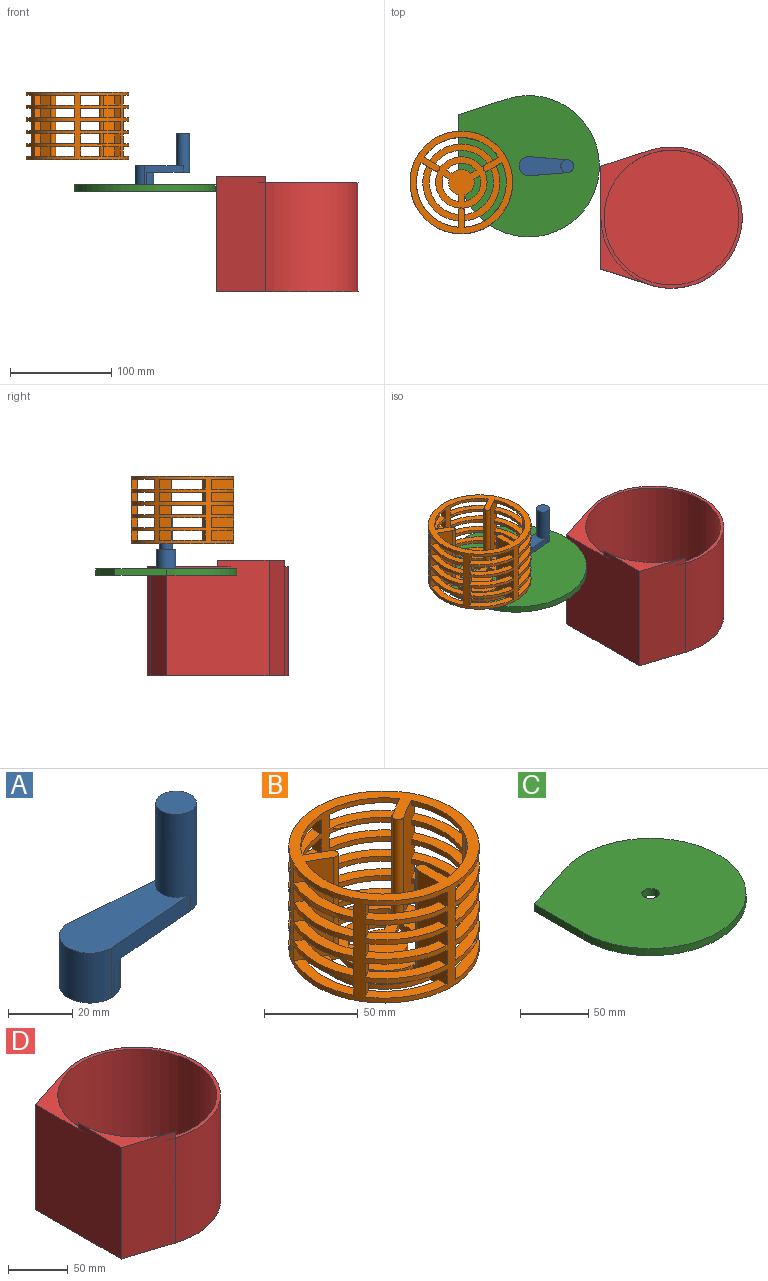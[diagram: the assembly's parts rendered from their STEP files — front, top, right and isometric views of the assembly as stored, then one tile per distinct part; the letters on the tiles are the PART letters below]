
ASSEMBLY  parts=4 mates=1
PART A: 11 faces, bbox 54x19.1x50.8 mm
  f0: cylinder r=6.35mm len=38.1mm, axis (0,0,-1), area 1393.4mm2, adj f1,f2,f3,f5,f6
  f1: plane 12.7x12.7mm, normal (0,0,1), area 126.7mm2, adj f0
  f2: plane 42.87x18.79mm, normal (0,0,-1), area 525.7mm2, adj f0,f3,f5,f7
  f3: plane 38.1x19.05mm, normal (0.08,1,0), area 262.9mm2, adj f0,f2,f4,f6,f7,f9
  f4: cylinder r=9.53mm len=19.05mm, axis (0,0,-1), area 570mm2, adj f3,f5,f6,f9
  f5: plane 38.1x19.05mm, normal (0.08,-1,0), area 262.9mm2, adj f0,f2,f4,f6,f7,f9
  f6: plane 47.63x19.05mm, normal (0,0,1), area 684mm2, adj f0,f3,f4,f5
  f7: cylinder r=9.53mm len=18.79mm, axis (0,0,1), area 339.8mm2, adj f2,f3,f5,f9
  f8: cylinder r=6.35mm len=12.7mm, axis (0,0,1), area 506.7mm2, adj f9,f10
  f9: plane 19.05x19.05mm, normal (0,0,-1), area 158.3mm2, adj f3,f4,f5,f7,f8
  f10: plane 12.7x12.7mm, normal (0,0,-1), area 126.7mm2, adj f8
PART B: 130 faces, bbox 101.6x101.6x66.7 mm
  f0: plane 66.68x22.08mm, normal (-0.5,-0.87,0), area 1350.8mm2, adj f46,f48,f50,f52,f54,f56,f58,f60
  f1: plane 66.68x22.08mm, normal (0.5,0.87,0), area 1350.8mm2, adj f26,f28,f30,f32,f34,f36,f38,f40
  f2: plane 66.68x22.08mm, normal (0.5,-0.87,0), area 1350.8mm2, adj f6,f8,f10,f12,f14,f16,f18,f20
  f3: plane 66.68x25.5mm, normal (-1,0,0), area 1350.8mm2, adj f45,f47,f49,f51,f53,f55,f57,f59
  f4: plane 66.68x22.08mm, normal (-0.5,0.87,0), area 1350.8mm2, adj f25,f27,f29,f31,f33,f35,f37,f39
  f5: plane 39.15x25.78mm, normal (0,0,1), area 276.3mm2, adj f67,f69,f73,f125
  f6: plane 45.2x10.82mm, normal (0,0,1), area 276.3mm2, adj f2,f67,f69,f126
  f7: plane 39.15x25.78mm, normal (0,0,1), area 276.3mm2, adj f67,f69,f73,f124
  f8: plane 45.2x10.82mm, normal (0,0,1), area 276.3mm2, adj f2,f67,f69,f123
  f9: plane 39.15x25.78mm, normal (0,0,-1), area 276.3mm2, adj f67,f69,f73,f125
  f10: plane 45.2x10.82mm, normal (0,0,-1), area 276.3mm2, adj f2,f67,f69,f126
  f11: plane 39.15x25.78mm, normal (0,0,1), area 276.3mm2, adj f67,f69,f73,f122
  f12: plane 45.2x10.82mm, normal (0,0,1), area 276.3mm2, adj f2,f67,f69,f121
  f13: plane 39.15x25.78mm, normal (0,0,-1), area 276.3mm2, adj f67,f69,f73,f124
  f14: plane 45.2x10.82mm, normal (0,0,-1), area 276.3mm2, adj f2,f67,f69,f123
  f15: plane 39.15x25.78mm, normal (0,0,-1), area 276.3mm2, adj f67,f69,f73,f122
  f16: plane 45.2x10.82mm, normal (0,0,-1), area 276.3mm2, adj f2,f67,f69,f121
  f17: plane 39.15x25.78mm, normal (0,0,1), area 276.3mm2, adj f67,f69,f73,f120
  f18: plane 45.2x10.82mm, normal (0,0,1), area 276.3mm2, adj f2,f67,f69,f119
  f19: plane 39.15x25.78mm, normal (0,0,1), area 276.3mm2, adj f67,f69,f73,f118
  f20: plane 45.2x10.82mm, normal (0,0,1), area 276.3mm2, adj f2,f67,f69,f117
  f21: plane 39.15x25.78mm, normal (0,0,-1), area 276.3mm2, adj f67,f69,f73,f120
  f22: plane 45.2x10.82mm, normal (0,0,-1), area 276.3mm2, adj f2,f67,f69,f119
  f23: plane 39.15x25.78mm, normal (0,0,-1), area 276.3mm2, adj f67,f69,f73,f118
  f24: plane 45.2x10.82mm, normal (0,0,-1), area 276.3mm2, adj f2,f67,f69,f117
  f25: plane 39.15x25.78mm, normal (0,0,1), area 276.3mm2, adj f4,f67,f90,f115
  f26: plane 39.15x25.78mm, normal (0,0,1), area 276.3mm2, adj f1,f67,f90,f116
  f27: plane 39.15x25.78mm, normal (0,0,1), area 276.3mm2, adj f4,f67,f90,f114
  f28: plane 39.15x25.78mm, normal (0,0,1), area 276.3mm2, adj f1,f67,f90,f113
  f29: plane 39.15x25.78mm, normal (0,0,-1), area 276.3mm2, adj f4,f67,f90,f115
  f30: plane 39.15x25.78mm, normal (0,0,-1), area 276.3mm2, adj f1,f67,f90,f116
  f31: plane 39.15x25.78mm, normal (0,0,1), area 276.3mm2, adj f4,f67,f90,f112
  f32: plane 39.15x25.78mm, normal (0,0,1), area 276.3mm2, adj f1,f67,f90,f111
  f33: plane 39.15x25.78mm, normal (0,0,-1), area 276.3mm2, adj f4,f67,f90,f114
  f34: plane 39.15x25.78mm, normal (0,0,-1), area 276.3mm2, adj f1,f67,f90,f113
  f35: plane 39.15x25.78mm, normal (0,0,-1), area 276.3mm2, adj f4,f67,f90,f112
  f36: plane 39.15x25.78mm, normal (0,0,-1), area 276.3mm2, adj f1,f67,f90,f111
  f37: plane 39.15x25.78mm, normal (0,0,1), area 276.3mm2, adj f4,f67,f90,f110
  f38: plane 39.15x25.78mm, normal (0,0,1), area 276.3mm2, adj f1,f67,f90,f109
  f39: plane 39.15x25.78mm, normal (0,0,1), area 276.3mm2, adj f4,f67,f90,f108
  f40: plane 39.15x25.78mm, normal (0,0,1), area 276.3mm2, adj f1,f67,f90,f107
  f41: plane 39.15x25.78mm, normal (0,0,-1), area 276.3mm2, adj f4,f67,f90,f110
  f42: plane 39.15x25.78mm, normal (0,0,-1), area 276.3mm2, adj f1,f67,f90,f109
  f43: plane 39.15x25.78mm, normal (0,0,-1), area 276.3mm2, adj f4,f67,f90,f108
  f44: plane 39.15x25.78mm, normal (0,0,-1), area 276.3mm2, adj f1,f67,f90,f107
  f45: plane 39.15x25.78mm, normal (0,0,1), area 276.3mm2, adj f3,f67,f95,f105
  f46: plane 45.2x10.82mm, normal (0,0,1), area 276.3mm2, adj f0,f67,f95,f106
  f47: plane 39.15x25.78mm, normal (0,0,-1), area 276.3mm2, adj f3,f67,f95,f103
  f48: plane 45.2x10.82mm, normal (0,0,-1), area 276.3mm2, adj f0,f67,f95,f104
  f49: plane 39.15x25.78mm, normal (0,0,1), area 276.3mm2, adj f3,f67,f95,f101
  f50: plane 45.2x10.82mm, normal (0,0,1), area 276.3mm2, adj f0,f67,f95,f102
  f51: plane 39.15x25.78mm, normal (0,0,-1), area 276.3mm2, adj f3,f67,f95,f105
  f52: plane 45.2x10.82mm, normal (0,0,-1), area 276.3mm2, adj f0,f67,f95,f106
  f53: plane 39.15x25.78mm, normal (0,0,1), area 276.3mm2, adj f3,f67,f95,f103
  f54: plane 45.2x10.82mm, normal (0,0,1), area 276.3mm2, adj f0,f67,f95,f104
  f55: plane 39.15x25.78mm, normal (0,0,-1), area 276.3mm2, adj f3,f67,f95,f101
  f56: plane 45.2x10.82mm, normal (0,0,-1), area 276.3mm2, adj f0,f67,f95,f102
  f57: plane 39.15x25.78mm, normal (0,0,1), area 276.3mm2, adj f3,f67,f95,f99
  f58: plane 45.2x10.82mm, normal (0,0,1), area 276.3mm2, adj f0,f67,f95,f100
  f59: plane 39.15x25.78mm, normal (0,0,1), area 276.3mm2, adj f3,f67,f95,f97
  f60: plane 45.2x10.82mm, normal (0,0,1), area 276.3mm2, adj f0,f67,f95,f98
  f61: plane 39.15x25.78mm, normal (0,0,-1), area 276.3mm2, adj f3,f67,f95,f99
  f62: plane 45.2x10.82mm, normal (0,0,-1), area 276.3mm2, adj f0,f67,f95,f100
  f63: plane 39.15x25.78mm, normal (0,0,-1), area 276.3mm2, adj f3,f67,f95,f97
  f64: plane 45.2x10.82mm, normal (0,0,-1), area 276.3mm2, adj f0,f67,f95,f98
  f65: plane 62.59x19.56mm, normal (0,0,1), area 424.1mm2, adj f1,f4,f89,f91
  f66: plane 54.2x34.93mm, normal (0,0,1), area 424.1mm2, adj f2,f70,f71,f73
  f67: cylinder r=50.8mm len=101.6mm, axis (0,0,1), area 7896.2mm2, adj f0,f1,f2,f3,f4,f5,f6,f7
  f68: plane 101.6x101.6mm, normal (0,0,-1), area 5051.2mm2, adj f0,f1,f2,f3,f4,f67,f69,f70
  f69: cylinder r=44.45mm len=66.68mm, axis (0,0,-1), area 1955.1mm2, adj f2,f5,f6,f7,f8,f9,f10,f11
  f70: cylinder r=38.1mm len=54.2mm, axis (0,0,-1), area 233.2mm2, adj f2,f66,f68,f73
  f71: cylinder r=31.75mm len=44.64mm, axis (0,0,-1), area 190.9mm2, adj f2,f66,f68,f73
  f72: cylinder r=25.4mm len=35.05mm, axis (0,0,-1), area 148.7mm2, adj f2,f68,f73,f88
  f73: plane 66.68x25.5mm, normal (1,0,0), area 1350.8mm2, adj f5,f7,f9,f11,f13,f15,f17,f19
  f74: cylinder r=25.4mm len=35.05mm, axis (0,0,-1), area 148.7mm2, adj f0,f3,f68,f88
  f75: cylinder r=25.4mm len=40.47mm, axis (0,0,-1), area 148.7mm2, adj f1,f4,f68,f88
  f76: plane 5.62x3.24mm, normal (0.5,0.87,0), area 20.6mm2, adj f68,f77,f79,f88
  f77: cylinder r=12.7mm len=18.12mm, axis (0,0,-1), area 64.1mm2, adj f68,f76,f78,f88
  f78: plane 5.62x3.24mm, normal (-0.5,0.87,0), area 20.6mm2, adj f68,f77,f79,f88
  f79: cylinder r=19.05mm len=29.36mm, axis (0,0,-1), area 106.4mm2, adj f68,f76,f78,f88
  f80: plane 6.49x3.18mm, normal (-1,0,0), area 20.6mm2, adj f68,f81,f83,f88
  f81: cylinder r=12.7mm len=15.7mm, axis (0,0,-1), area 64.1mm2, adj f68,f80,f82,f88
  f82: plane 5.62x3.24mm, normal (-0.5,-0.87,0), area 20.6mm2, adj f68,f81,f83,f88
  f83: cylinder r=19.05mm len=25.43mm, axis (0,0,-1), area 106.4mm2, adj f68,f80,f82,f88
  f84: cylinder r=12.7mm len=15.7mm, axis (0,0,-1), area 64.1mm2, adj f68,f85,f87,f88
  f85: plane 6.49x3.18mm, normal (1,0,0), area 20.6mm2, adj f68,f84,f86,f88
  f86: cylinder r=19.05mm len=25.43mm, axis (0,0,-1), area 106.4mm2, adj f68,f85,f87,f88
  f87: plane 5.62x3.24mm, normal (0.5,-0.87,0), area 20.6mm2, adj f68,f84,f86,f88
  f88: plane 53.88x52.5mm, normal (0,0,1), area 1527.6mm2, adj f0,f1,f2,f3,f4,f72,f73,f74
  f89: cylinder r=38.1mm len=62.59mm, axis (0,0,-1), area 233.2mm2, adj f1,f4,f65,f68
  f90: cylinder r=44.45mm len=73.62mm, axis (0,0,-1), area 1955.1mm2, adj f1,f4,f25,f26,f27,f28,f29,f30
  f91: cylinder r=31.75mm len=51.54mm, axis (0,0,-1), area 190.9mm2, adj f1,f4,f65,f68
  f92: plane 54.2x34.93mm, normal (0,0,1), area 424.1mm2, adj f0,f3,f93,f94
  f93: cylinder r=38.1mm len=54.2mm, axis (0,0,-1), area 233.2mm2, adj f0,f3,f68,f92
  f94: cylinder r=31.75mm len=44.64mm, axis (0,0,-1), area 190.9mm2, adj f0,f3,f68,f92
  f95: cylinder r=44.45mm len=66.68mm, axis (0,0,-1), area 1955.1mm2, adj f0,f3,f45,f46,f47,f48,f49,f50
  f96: plane 101.6x101.6mm, normal (0,0,1), area 2251.2mm2, adj f0,f1,f2,f3,f4,f67,f69,f73
  f97: plane 9.53x5.51mm, normal (0.5,-0.87,0), area 60.6mm2, adj f59,f63,f67,f95
  f98: plane 9.53x5.51mm, normal (-0.5,0.87,0), area 60.6mm2, adj f60,f64,f67,f95
  f99: plane 9.53x5.51mm, normal (0.5,-0.87,0), area 60.6mm2, adj f57,f61,f67,f95
  f100: plane 9.53x5.51mm, normal (-0.5,0.87,0), area 60.6mm2, adj f58,f62,f67,f95
  f101: plane 9.53x5.51mm, normal (0.5,-0.87,0), area 60.6mm2, adj f49,f55,f67,f95
  f102: plane 9.53x5.51mm, normal (-0.5,0.87,0), area 60.6mm2, adj f50,f56,f67,f95
  f103: plane 9.53x5.51mm, normal (0.5,-0.87,0), area 60.6mm2, adj f47,f53,f67,f95
  f104: plane 9.53x5.51mm, normal (-0.5,0.87,0), area 60.6mm2, adj f48,f54,f67,f95
  f105: plane 9.53x5.51mm, normal (0.5,-0.87,0), area 60.6mm2, adj f45,f51,f67,f95
  f106: plane 9.53x5.51mm, normal (-0.5,0.87,0), area 60.6mm2, adj f46,f52,f67,f95
  f107: plane 9.53x6.36mm, normal (-1,0,0), area 60.6mm2, adj f40,f44,f67,f90
  f108: plane 9.53x6.36mm, normal (1,0,0), area 60.6mm2, adj f39,f43,f67,f90
  f109: plane 9.53x6.36mm, normal (-1,0,0), area 60.6mm2, adj f38,f42,f67,f90
  f110: plane 9.53x6.36mm, normal (1,0,0), area 60.6mm2, adj f37,f41,f67,f90
  f111: plane 9.53x6.36mm, normal (-1,0,0), area 60.6mm2, adj f32,f36,f67,f90
  f112: plane 9.53x6.36mm, normal (1,0,0), area 60.6mm2, adj f31,f35,f67,f90
  f113: plane 9.53x6.36mm, normal (-1,0,0), area 60.6mm2, adj f28,f34,f67,f90
  f114: plane 9.53x6.36mm, normal (1,0,0), area 60.6mm2, adj f27,f33,f67,f90
  f115: plane 9.53x6.36mm, normal (1,0,0), area 60.6mm2, adj f25,f29,f67,f90
  f116: plane 9.53x6.36mm, normal (-1,0,0), area 60.6mm2, adj f26,f30,f67,f90
  f117: plane 9.53x5.51mm, normal (0.5,0.87,0), area 60.6mm2, adj f20,f24,f67,f69
  f118: plane 9.53x5.51mm, normal (-0.5,-0.87,0), area 60.6mm2, adj f19,f23,f67,f69
  f119: plane 9.53x5.51mm, normal (0.5,0.87,0), area 60.6mm2, adj f18,f22,f67,f69
  f120: plane 9.53x5.51mm, normal (-0.5,-0.87,0), area 60.6mm2, adj f17,f21,f67,f69
  f121: plane 9.53x5.51mm, normal (0.5,0.87,0), area 60.6mm2, adj f12,f16,f67,f69
  f122: plane 9.53x5.51mm, normal (-0.5,-0.87,0), area 60.6mm2, adj f11,f15,f67,f69
  f123: plane 9.53x5.51mm, normal (0.5,0.87,0), area 60.6mm2, adj f8,f14,f67,f69
  f124: plane 9.53x5.51mm, normal (-0.5,-0.87,0), area 60.6mm2, adj f7,f13,f67,f69
  f125: plane 9.53x5.51mm, normal (-0.5,-0.87,0), area 60.6mm2, adj f5,f9,f67,f69
  f126: plane 9.53x5.51mm, normal (0.5,0.87,0), area 60.6mm2, adj f6,f10,f67,f69
  f127: cylinder r=3.17mm len=63.5mm, axis (0,0,-1), area 633.4mm2, adj f3,f73,f88,f96
  f128: cylinder r=3.17mm len=63.5mm, axis (0,0,1), area 633.4mm2, adj f2,f4,f88,f96
  f129: cylinder r=3.17mm len=63.5mm, axis (0,0,-1), area 633.4mm2, adj f0,f1,f88,f96
PART C: 6 faces, bbox 139.7x139.7x6.4 mm
  f0: plane 50.8x6.35mm, normal (-1,0,0), area 322.6mm2, adj f1,f2,f3,f4
  f1: cylinder r=69.85mm len=139.7mm, axis (0,0,-1), area 2229.1mm2, adj f0,f2,f3,f4
  f2: plane 48.33x15.65mm, normal (-0.31,0.95,0), area 322.6mm2, adj f0,f1,f3,f4
  f3: plane 139.7x139.7mm, normal (0,0,1), area 15681.7mm2, adj f0,f1,f2,f5
  f4: plane 139.7x139.7mm, normal (0,0,-1), area 15681.7mm2, adj f0,f1,f2,f5
  f5: cylinder r=6.35mm len=12.7mm, axis (0,0,1), area 253.4mm2, adj f3,f4
PART D: 10 faces, bbox 139.7x139.7x114.3 mm
  f0: plane 139.7x139.7mm, normal (0,0,1), area 1842.2mm2, adj f2,f3,f5,f6,f8
  f1: plane 133.35x133.35mm, normal (0,0,1), area 13966.1mm2, adj f6
  f2: plane 107.95x48.33mm, normal (-0.31,0.95,0), area 5483.9mm2, adj f0,f3,f5,f7
  f3: plane 114.3x101.6mm, normal (-1,0,0), area 11290.3mm2, adj f0,f2,f4,f7,f8,f9
  f4: plane 114.3x48.33mm, normal (-0.31,-0.95,0), area 5806.4mm2, adj f3,f5,f7,f8,f9
  f5: cylinder r=69.85mm len=139.7mm, axis (0,0,-1), area 28411.9mm2, adj f0,f2,f4,f7
  f6: cylinder r=66.67mm len=133.35mm, axis (0,0,-1), area 42563.4mm2, adj f0,f1
  f7: plane 139.7x139.7mm, normal (0,0,-1), area 16288.8mm2, adj f2,f3,f4,f5
  f8: cylinder r=69.85mm len=66.45mm, axis (0,0,-1), area 557.8mm2, adj f0,f3,f4,f9
  f9: plane 66.45x48.33mm, normal (0,0,1), area 480.5mm2, adj f3,f4,f8
PLACE A t=(22.86,-30.59,-93.51)mm
PLACE B t=(-43.71,-46.72,39.52)mm
PLACE C t=(22.86,-30.59,-220.51)mm
PLACE D t=(164.04,-81.35,-211.87)mm
MATE fastened C.f1 <-> A.f4  axis (0,0,1) through (22.86,-30.59,-106.21)mm
